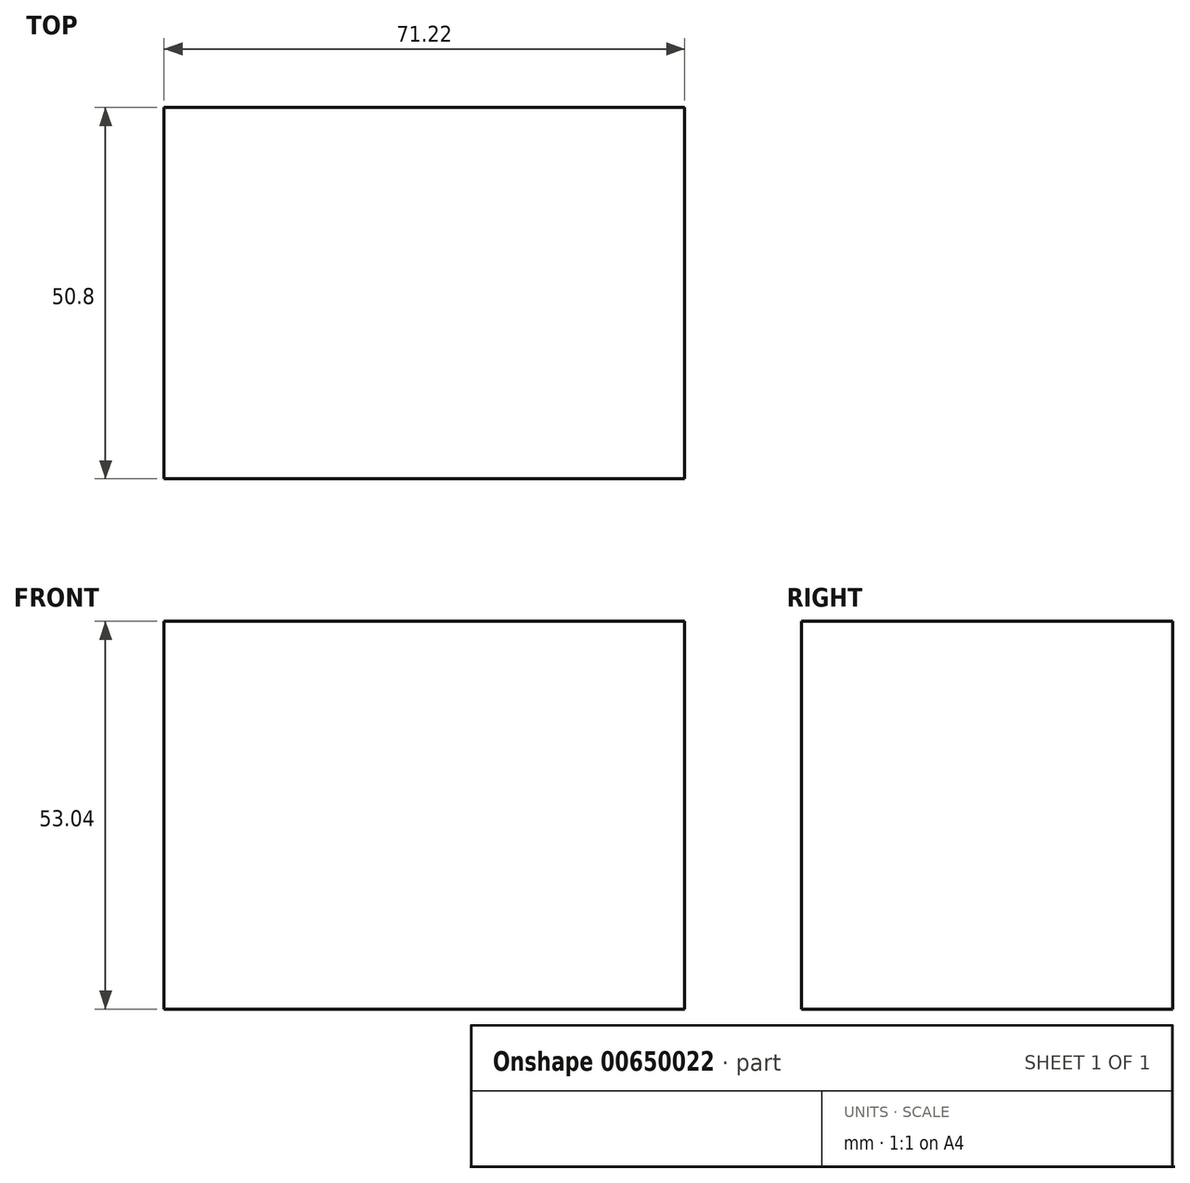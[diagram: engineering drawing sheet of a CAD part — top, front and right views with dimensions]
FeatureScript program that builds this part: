
annotation { "Feature Type Name" : "Feature", "Feature Type Description" : "" }
export const myFeature = defineFeature(function(context is Context, id is Id, definition is map)
    precondition{}
    {
        {
            var Q0;
            Q0=qCreatedBy(makeId("Front.planeOp"),FACE);
            var sketch = newSketch(context, id + "F0", { "sketchPlane" : qUnion([Q0])});
            skLineSegment(sketch, "E0.bottom", {"start": v(-35.61, -26.52) * mm, "end": v(35.61, -26.52) * mm});
            skLineSegment(sketch, "E0.top", {"start": v(-35.61, 26.52) * mm, "end": v(35.61, 26.52) * mm});
            skLineSegment(sketch, "E0.left", {"start": v(-35.61, -26.52) * mm, "end": v(-35.61, 26.52) * mm});
            skLineSegment(sketch, "E0.right", {"start": v(35.61, -26.52) * mm, "end": v(35.61, 26.52) * mm});
            skPoint(sketch, "E0.middle", {"position": v(0, 0) * mm});
            skSolve(sketch);
        }
        {
            var Q0;
            Q0 = qSketchRegion(id + "F0", true);
            extrude(context, id + "F1", {"entities" : qUnion([Q0]), "depth" : 50.8 * mm, "offsetDistance" : 25.4 * mm});
        }
    });
